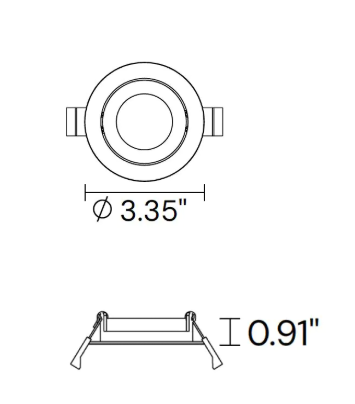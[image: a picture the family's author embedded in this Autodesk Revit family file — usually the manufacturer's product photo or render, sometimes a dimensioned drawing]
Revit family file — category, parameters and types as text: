
# Revit family: Alcon-14133-6 -Revit-Family
name_source: partatom
category: Lighting Fixtures
units: mm (PartAtom-declared; Revit-internal decimal feet)

## family parameters
Always vertical = Yes
Cut with Voids When Loaded = No
Host = Ceiling
Light Source = Yes
OmniClass Number = 23.80.70.11
OmniClass Title = Luminaries for Internal Lighting
Part Type = Normal
Room Calculation Point = No
Round Connector Dimension = Use Diameter
Shared = No

## types (1)
- Type 1
    Color Filter = 16777215
    Default Elevation = 0' - 0"
    Dimming Lamp Color Temperature Shift = <None>
    Emit Shape Visible in Rendering = No
    Emit from Circle Diameter = 0' - 6"
    Housing = Default
    Lens = Default
    Light Source Symbol Length = 10' - 0"
    LightSource = light
    Link To Product Page = https://www.alconlighting.com
    Manufacturer = Alcon Light
    Metal = <By Category>
    Product Identity = Alcon Lighting 14133-6
    Reflector = Default metal
    Spot Beam Angle = 30.00°
    Spot Field Angle = 90.00°
    Tilt Angle = 90.00°

## geometry (parser evidence)
native form markers: Sweep x2
no freeform markers — native parametric forms only
